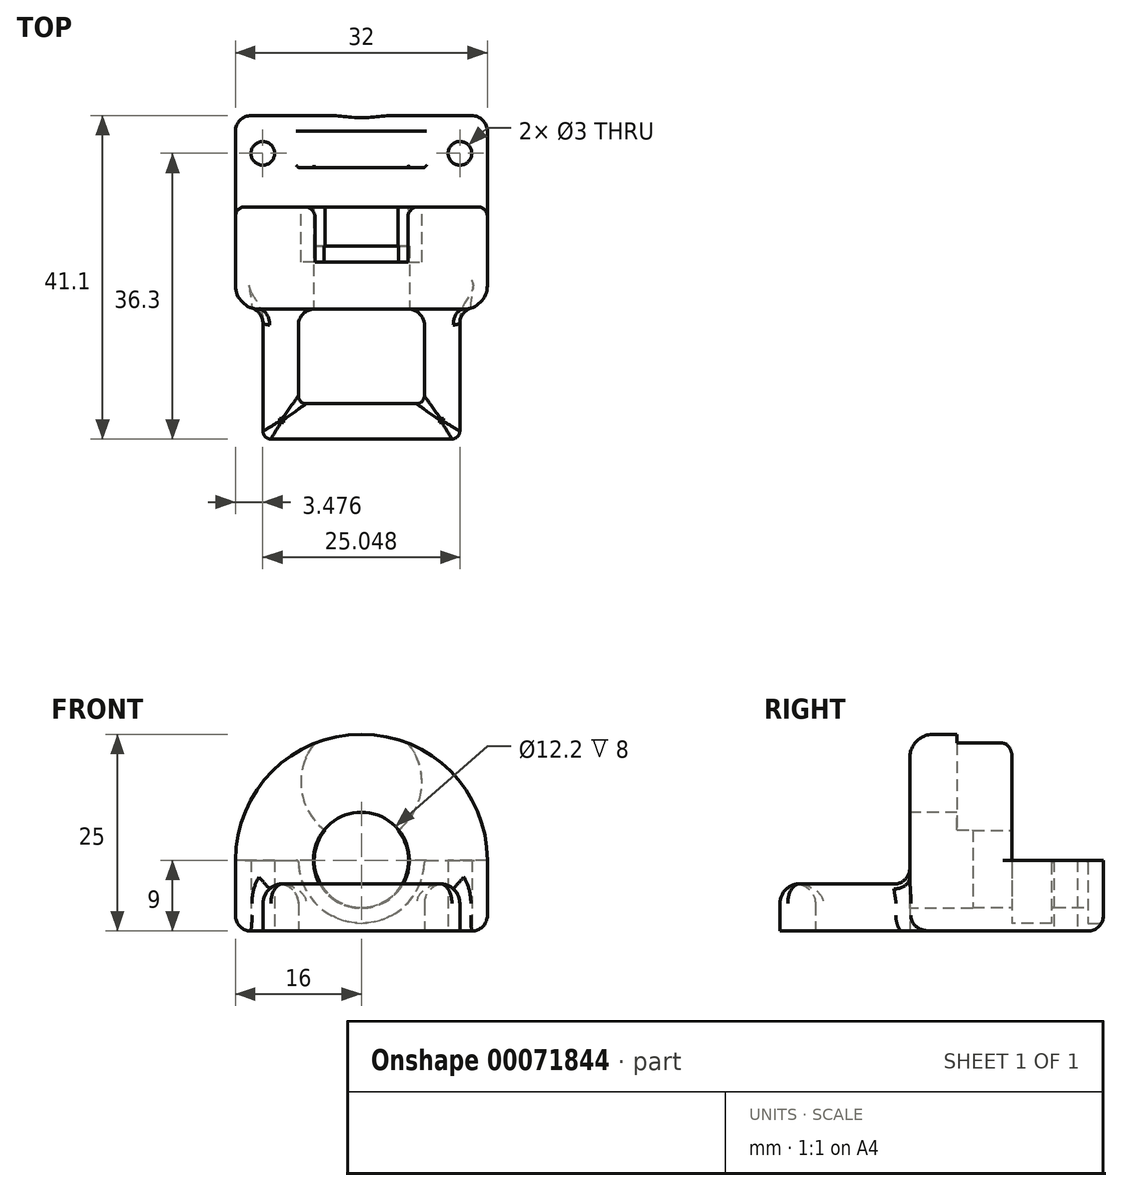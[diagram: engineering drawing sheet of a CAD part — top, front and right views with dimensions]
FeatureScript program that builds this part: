
annotation { "Feature Type Name" : "Feature", "Feature Type Description" : "" }
export const myFeature = defineFeature(function(context is Context, id is Id, definition is map)
    precondition{}
    {
        {
            var Q0;
            Q0=qCreatedBy(makeId("Top.planeOp"),FACE);
            var sketch = newSketch(context, id + "F0", { "sketchPlane" : qUnion([Q0])});
            skLineSegment(sketch, "E0.rect.bottom", {"start": v(-16, 5.8) * mm, "end": v(16, 5.8) * mm});
            skLineSegment(sketch, "E0.rect.top", {"start": v(-16, -5.8) * mm, "end": v(16, -5.8) * mm});
            skLineSegment(sketch, "E0.rect.left", {"start": v(-16, 5.8) * mm, "end": v(-16, -5.8) * mm});
            skLineSegment(sketch, "E0.rect.right", {"start": v(16, 5.8) * mm, "end": v(16, -5.8) * mm});
            skPoint(sketch, "E0.rect.middle", {"position": v(0, 0) * mm});
            skCircle(sketch, "E1", {"center": v(12.52, 1) * mm, "radius": 1.5 * mm});
            skCircle(sketch, "E2", {"center": v(-12.52, 1) * mm, "radius": 1.5 * mm});
            skSolve(sketch);
        }
        {
            var Q0;
            Q0=makeQuery(id+"F0.imprint","IMPRINT",FACE,{"disambiguationData":[TD([[makeQuery(id+"F0.imprint","IMPRINT",EDGE,{"derivedFrom":sQuery(id+"F0.wireOp",EDGE,"E0.rect.bottom")}),-1.0]])]});
            extrude(context, id + "F1", {"entities" : qUnion([Q0]), "depth" : 9 * mm});
        }
        {
            var Q0;
            Q0=makeQuery(id+"F1.opExtrude","SWEPT_FACE",FACE,{"disambiguationData":[OSD([sQuery(id+"F0.wireOp",EDGE,"E0.rect.top")])]});
            var sketch = newSketch(context, id + "F2", { "sketchPlane" : qUnion([Q0])});
            skCircle(sketch, "E3", {"center": v(0, 9) * mm, "radius": 8 * mm});
            skSolve(sketch);
        }
        {
            var Q0;
            Q0=qSketchRegion(id+"F2",true);
            var Q1;
            Q1=makeQuery(id+"F1.opExtrude","SWEPT_FACE",FACE,{"disambiguationData":[OSD([sQuery(id+"F0.wireOp",EDGE,"E0.rect.bottom")])]});
            extrude(context, id + "F3", {"entities" : qUnion([Q0, Q1]), "operationType" : NewBodyOperationType.REMOVE, "oppositeDirection" : true, "depth" : 5 * mm});
        }
        {
            var Q0;
            Q0=makeQuery(id+"F1.opExtrude","SWEPT_FACE",FACE,{"disambiguationData":[OSD([sQuery(id+"F0.wireOp",EDGE,"E0.rect.bottom")])]});
            var sketch = newSketch(context, id + "F4", { "sketchPlane" : qUnion([Q0])});
            skCircle(sketch, "E4", {"center": v(0, 9) * mm, "radius": 8 * mm});
            skSolve(sketch);
        }
        {
            var Q0;
            Q0=qSketchRegion(id+"F4",true);
            extrude(context, id + "F5", {"entities" : qUnion([Q0]), "operationType" : NewBodyOperationType.REMOVE, "oppositeDirection" : true, "depth" : 2 * mm});
        }
        {
            var Q0;
            Q0=makeQuery(id+"F5.boolean.opBoolean","COPY",FACE,{"derivedFrom":makeQuery(id+"F5.opExtrude","CAP_FACE",FACE,{"disambiguationData":[OSD([sQuery(id+"F4.wireOp",EDGE,"E4")])],"isStart":false})});
            var sketch = newSketch(context, id + "F6", { "sketchPlane" : qUnion([Q0])});
            skCircle(sketch, "E5", {"center": v(0, 9) * mm, "radius": 6 * mm});
            skSolve(sketch);
        }
        {
            var Q0;
            Q0=qSketchRegion(id+"F6",true);
            extrude(context, id + "F7", {"entities" : qUnion([Q0]), "operationType" : NewBodyOperationType.REMOVE, "oppositeDirection" : true, "depth" : 25 * mm});
        }
        {
            var Q0;
            Q0=makeQuery(id+"F1.opExtrude","SWEPT_FACE",FACE,{"disambiguationData":[OSD([sQuery(id+"F0.wireOp",EDGE,"E0.rect.top")])]});
            var sketch = newSketch(context, id + "F8", { "sketchPlane" : qUnion([Q0])});
            skArc(sketch, "E6", {"start": v(16, 9) * mm, "mid": v(0, 25) * mm, "end": v(-16, 9) * mm});
            skLineSegment(sketch, "E7", {"start": v(0, 0) * mm, "end": v(13.23, 0) * mm});
            skLineSegment(sketch, "E8", {"start": v(-13.23, 0) * mm, "end": v(0, 0) * mm});
            skLineSegment(sketch, "E9", {"start": v(-16, 9) * mm, "end": v(-16, 0) * mm});
            skLineSegment(sketch, "E10", {"start": v(16, 9) * mm, "end": v(16, 0) * mm});
            skLineSegment(sketch, "E11", {"start": v(-16, 0) * mm, "end": v(16, 0) * mm});
            skSolve(sketch);
        }
        {
            var Q0;
            Q0=qSketchRegion(id+"F8",true);
            extrude(context, id + "F9", {"entities" : qUnion([Q0]), "operationType" : NewBodyOperationType.ADD, "depth" : 13 * mm});
        }
        {
            var Q0;
            Q0=qCreatedBy(makeId("Top.planeOp"),FACE);
            var sketch = newSketch(context, id + "F10", { "sketchPlane" : qUnion([Q0])});
            skLineSegment(sketch, "E12", {"start": v(-8, -18.8) * mm, "end": v(-12.5, -18.8) * mm});
            skLineSegment(sketch, "E13", {"start": v(-12.5, -18.8) * mm, "end": v(-8, -18.8) * mm});
            skLineSegment(sketch, "E14", {"start": v(12.5, -18.8) * mm, "end": v(12.5, -35.3) * mm});
            skLineSegment(sketch, "E15", {"start": v(12.5, -35.3) * mm, "end": v(-12.5, -35.3) * mm});
            skLineSegment(sketch, "E16", {"start": v(-12.5, -35.3) * mm, "end": v(-12.5, -18.8) * mm});
            skLineSegment(sketch, "E17", {"start": v(-8, -18.8) * mm, "end": v(-8, -30.8) * mm});
            skLineSegment(sketch, "E18", {"start": v(-8, -30.8) * mm, "end": v(8, -30.8) * mm});
            skLineSegment(sketch, "E19", {"start": v(8, -30.8) * mm, "end": v(8, -18.8) * mm});
            skLineSegment(sketch, "E20.trimOffspring", {"start": v(8, -18.8) * mm, "end": v(12.5, -18.8) * mm});
            skPoint(sketch, "E21.orphan", {"position": v(0, -18.8) * mm});
            skPoint(sketch, "E22", {"position": v(0, -30.8) * mm});
            skPoint(sketch, "E23", {"position": v(0, -35.3) * mm});
            skSolve(sketch);
        }
        {
            var Q0;
            Q0=qSketchRegion(id+"F10",true);
            extrude(context, id + "F11", {"entities" : qUnion([Q0]), "operationType" : NewBodyOperationType.ADD, "depth" : 6 * mm});
        }
        {
            var Q0;
            Q0=makeQuery(id+"F11.opExtrude","CAP_EDGE",EDGE,{"disambiguationData":[OSD([sQuery(id+"F10.wireOp",EDGE,"E17")])],"isStart":false});
            var Q1;
            Q1=makeQuery(id+"F11.opExtrude","CAP_EDGE",EDGE,{"disambiguationData":[OSD([sQuery(id+"F10.wireOp",EDGE,"E16")])],"isStart":false});
            var Q2;
            Q2=makeQuery(id+"F11.opExtrude","CAP_EDGE",EDGE,{"disambiguationData":[OSD([sQuery(id+"F10.wireOp",EDGE,"E19")])],"isStart":false});
            var Q3;
            Q3=makeQuery(id+"F11.opExtrude","CAP_EDGE",EDGE,{"disambiguationData":[OSD([sQuery(id+"F10.wireOp",EDGE,"E14")])],"isStart":false});
            var Q4;
            Q4=makeQuery(id+"F11.opExtrude","CAP_EDGE",EDGE,{"disambiguationData":[OSD([sQuery(id+"F10.wireOp",EDGE,"E18")])],"isStart":false});
            var Q5;
            Q5=makeQuery(id+"F11.opExtrude","CAP_EDGE",EDGE,{"disambiguationData":[OSD([sQuery(id+"F10.wireOp",EDGE,"E15")])],"isStart":false});
            fillet(context, id + "F12", {"entities" : qUnion([Q0, Q1, Q2, Q3, Q4, Q5]), "radius" : 2.5 * mm, "tangentPropagation" : true, "allowEdgeOverflow" : false});
        }
        {
            var Q0;
            Q0=makeQuery(id+"F9.opExtrude","CAP_EDGE",EDGE,{"disambiguationData":[OSD([sQuery(id+"F8.wireOp",EDGE,"E6")])],"isStart":false});
            fillet(context, id + "F13", {"entities" : qUnion([Q0]), "radius" : 3 * mm, "tangentPropagation" : true, "allowEdgeOverflow" : false});
        }
        {
            var Q0;
            Q0=makeQuery(id+"F9.opExtrude","CAP_EDGE",EDGE,{"disambiguationData":[OSD([sQuery(id+"F8.wireOp",EDGE,"E6")])],"isStart":true});
            fillet(context, id + "F14", {"entities" : qUnion([Q0]), "radius" : 1.2 * mm, "tangentPropagation" : true, "allowEdgeOverflow" : false});
        }
        {
            var Q0;
            Q0=makeQuery(id+"F9.opExtrude","CAP_FACE",FACE,{"disambiguationData":[OSD([sQuery(id+"F8.wireOp",EDGE,"E6"),sQuery(id+"F8.wireOp",EDGE,"E9"),sQuery(id+"F8.wireOp",EDGE,"E10"),sQuery(id+"F8.wireOp",EDGE,"E11")])],"isStart":false});
            var sketch = newSketch(context, id + "F15", { "sketchPlane" : qUnion([Q0])});
            skCircle(sketch, "E24", {"center": v(0, 9) * mm, "radius": 6.1 * mm});
            skSolve(sketch);
        }
        {
            var Q0;
            Q0=qSketchRegion(id+"F15",true);
            extrude(context, id + "F16", {"entities" : qUnion([Q0]), "operationType" : NewBodyOperationType.REMOVE, "oppositeDirection" : true, "depth" : 8 * mm});
        }
        {
            var Q0;
            Q0=makeQuery(id+"F13.opFillet","BLEND_EDGE",EDGE,{"blendedFrom":[makeQuery(id+"F9.opExtrude","CAP_EDGE",EDGE,{"disambiguationData":[OSD([sQuery(id+"F8.wireOp",EDGE,"E9")])],"isStart":false}),makeQuery(id+"F9.boolean.opBoolean","MERGE",FACE,{"derivedFrom":[makeQuery(id+"F1.opExtrude","CAP_FACE",FACE,{"disambiguationData":[OSD([sQuery(id+"F0.wireOp",EDGE,"E0.rect.bottom"),sQuery(id+"F0.wireOp",EDGE,"E0.rect.top"),sQuery(id+"F0.wireOp",EDGE,"E0.rect.left"),sQuery(id+"F0.wireOp",EDGE,"E0.rect.right"),sQuery(id+"F0.wireOp",EDGE,"E1"),sQuery(id+"F0.wireOp",EDGE,"E2")])],"isStart":true}),makeQuery(id+"F9.opExtrude","SWEPT_FACE",FACE,{"disambiguationData":[OSD([sQuery(id+"F8.wireOp",EDGE,"E11")])]})]})],"blendedInto":[makeQuery(id+"F9.boolean.opBoolean","MERGE",FACE,{"derivedFrom":[makeQuery(id+"F1.opExtrude","CAP_FACE",FACE,{"disambiguationData":[OSD([sQuery(id+"F0.wireOp",EDGE,"E0.rect.bottom"),sQuery(id+"F0.wireOp",EDGE,"E0.rect.top"),sQuery(id+"F0.wireOp",EDGE,"E0.rect.left"),sQuery(id+"F0.wireOp",EDGE,"E0.rect.right"),sQuery(id+"F0.wireOp",EDGE,"E1"),sQuery(id+"F0.wireOp",EDGE,"E2")])],"isStart":true}),makeQuery(id+"F9.opExtrude","SWEPT_FACE",FACE,{"disambiguationData":[OSD([sQuery(id+"F8.wireOp",EDGE,"E11")])]})]})]});
            fillet(context, id + "F17", {"entities" : qUnion([Q0]), "radius" : 2 * mm, "tangentPropagation" : true, "allowEdgeOverflow" : false});
        }
        {
            var Q0;
            {var subQ0=sQuery(id+"F8.wireOp",EDGE,"E6");var subQ1=sQuery(id+"F8.wireOp",EDGE,"E9");var subQ2=sQuery(id+"F8.wireOp",EDGE,"E10");Q0=makeQuery(id+"F9.boolean.opBoolean","SPLIT",FACE,{"disambiguationData":[TD([makeQuery(id+"F3.boolean.opBoolean","COPY",FACE,{"derivedFrom":makeQuery(id+"F3.opExtrude","SWEPT_FACE",FACE,{"disambiguationData":[OSD([sQuery(id+"F2.wireOp",EDGE,"E3")])]})})])],"derivedFrom":makeQuery(id+"F9.opExtrude","CAP_FACE",FACE,{"disambiguationData":[OSD([subQ0,subQ1,subQ2,sQuery(id+"F8.wireOp",EDGE,"E11")])],"isStart":true})});}
            var sketch = newSketch(context, id + "F18", { "sketchPlane" : qUnion([Q0])});
            skCircle(sketch, "E25", {"center": v(0, 9) * mm, "radius": 6 * mm});
            skCircle(sketch, "E26", {"center": v(0, 18.94) * mm, "radius": 7.69 * mm});
            skSolve(sketch);
        }
        {
            var Q0;
            Q0=makeQuery(id+"F1.opExtrude","CAP_EDGE",EDGE,{"disambiguationData":[OSD([sQuery(id+"F0.wireOp",EDGE,"E0.rect.bottom")])],"isStart":true});
            var Q1;
            Q1=makeQuery(id+"F7.boolean.opBoolean","COPY",EDGE,{"derivedFrom":makeQuery(id+"F7.opExtrude","CAP_EDGE",EDGE,{"disambiguationData":[OSD([sQuery(id+"F6.wireOp",EDGE,"E5")])],"isStart":true})});
            var Q2;
            Q2=makeQuery(id+"F1.opExtrude","SWEPT_EDGE",EDGE,{"disambiguationData":[OSD([sQuery(id+"F0.wireOp",EDGE,"E0.rect.bottom"),sQuery(id+"F0.wireOp",EDGE,"E0.rect.left")])]});
            var Q3;
            Q3=makeQuery(id+"F1.opExtrude","CAP_EDGE",EDGE,{"disambiguationData":[OSD([sQuery(id+"F0.wireOp",EDGE,"E0.rect.left")])],"isStart":true});
            var Q4;
            Q4=makeQuery(id+"F1.opExtrude","SWEPT_EDGE",EDGE,{"disambiguationData":[OSD([sQuery(id+"F0.wireOp",EDGE,"E0.rect.bottom"),sQuery(id+"F0.wireOp",EDGE,"E0.rect.right")])]});
            var Q5;
            Q5=makeQuery(id+"F1.opExtrude","CAP_EDGE",EDGE,{"disambiguationData":[OSD([sQuery(id+"F0.wireOp",EDGE,"E0.rect.right")])],"isStart":true});
            fillet(context, id + "F19", {"entities" : qUnion([Q0, Q1, Q2, Q3, Q4, Q5]), "radius" : 2 * mm, "tangentPropagation" : true, "allowEdgeOverflow" : false});
        }
        {
            var Q0;
            Q0=qSketchRegion(id+"F18",true);
            extrude(context, id + "F20", {"entities" : qUnion([Q0]), "operationType" : NewBodyOperationType.REMOVE, "oppositeDirection" : true, "depth" : 7 * mm});
        }
        {
            var Q0;
            Q0=makeQuery(id+"F12.opFillet","BLEND_EDGE",EDGE,{"blendedFrom":[makeQuery(id+"F11.opExtrude","CAP_EDGE",EDGE,{"disambiguationData":[OSD([sQuery(id+"F10.wireOp",EDGE,"E14")])],"isStart":false}),makeQuery(id+"F11.opExtrude","CAP_EDGE",EDGE,{"disambiguationData":[OSD([sQuery(id+"F10.wireOp",EDGE,"E15")])],"isStart":false})],"blendedInto":[]});
            var Q1;
            Q1=makeQuery(id+"F12.opFillet","BLEND_EDGE",EDGE,{"blendedFrom":[makeQuery(id+"F11.opExtrude","CAP_EDGE",EDGE,{"disambiguationData":[OSD([sQuery(id+"F10.wireOp",EDGE,"E18")])],"isStart":false}),makeQuery(id+"F11.opExtrude","CAP_EDGE",EDGE,{"disambiguationData":[OSD([sQuery(id+"F10.wireOp",EDGE,"E19")])],"isStart":false})],"blendedInto":[]});
            var Q2;
            Q2=makeQuery(id+"F12.opFillet","BLEND_EDGE",EDGE,{"blendedFrom":[makeQuery(id+"F11.opExtrude","CAP_EDGE",EDGE,{"disambiguationData":[OSD([sQuery(id+"F10.wireOp",EDGE,"E14")])],"isStart":false}),makeQuery(id+"F11.opExtrude","CAP_EDGE",EDGE,{"disambiguationData":[OSD([sQuery(id+"F10.wireOp",EDGE,"E19")])],"isStart":false})],"blendedInto":[]});
            var Q3;
            Q3=makeQuery(id+"F12.opFillet","BLEND_EDGE",EDGE,{"blendedFrom":[makeQuery(id+"F11.opExtrude","CAP_EDGE",EDGE,{"disambiguationData":[OSD([sQuery(id+"F10.wireOp",EDGE,"E15")])],"isStart":false}),makeQuery(id+"F11.opExtrude","CAP_EDGE",EDGE,{"disambiguationData":[OSD([sQuery(id+"F10.wireOp",EDGE,"E18")])],"isStart":false})],"blendedInto":[]});
            var Q4;
            Q4=makeQuery(id+"F12.opFillet","BLEND_EDGE",EDGE,{"blendedFrom":[makeQuery(id+"F11.opExtrude","CAP_EDGE",EDGE,{"disambiguationData":[OSD([sQuery(id+"F10.wireOp",EDGE,"E16")])],"isStart":false}),makeQuery(id+"F11.opExtrude","CAP_EDGE",EDGE,{"disambiguationData":[OSD([sQuery(id+"F10.wireOp",EDGE,"E17")])],"isStart":false})],"blendedInto":[]});
            var Q5;
            Q5=makeQuery(id+"F12.opFillet","BLEND_EDGE",EDGE,{"blendedFrom":[makeQuery(id+"F11.opExtrude","CAP_EDGE",EDGE,{"disambiguationData":[OSD([sQuery(id+"F10.wireOp",EDGE,"E15")])],"isStart":false}),makeQuery(id+"F11.opExtrude","CAP_EDGE",EDGE,{"disambiguationData":[OSD([sQuery(id+"F10.wireOp",EDGE,"E16")])],"isStart":false})],"blendedInto":[]});
            var Q6;
            Q6=makeQuery(id+"F12.opFillet","BLEND_EDGE",EDGE,{"blendedFrom":[makeQuery(id+"F11.opExtrude","CAP_EDGE",EDGE,{"disambiguationData":[OSD([sQuery(id+"F10.wireOp",EDGE,"E17")])],"isStart":false}),makeQuery(id+"F11.opExtrude","CAP_EDGE",EDGE,{"disambiguationData":[OSD([sQuery(id+"F10.wireOp",EDGE,"E18")])],"isStart":false})],"blendedInto":[]});
            fillet(context, id + "F21", {"entities" : qUnion([Q0, Q1, Q2, Q3, Q4, Q5, Q6]), "radius" : 1 * mm, "tangentPropagation" : true, "allowEdgeOverflow" : false});
        }
        {
            var Q0;
            Q0=makeQuery(id+"F12.opFillet","BLEND_EDGE",EDGE,{"blendedFrom":[makeQuery(id+"F11.opExtrude","CAP_EDGE",EDGE,{"disambiguationData":[OSD([sQuery(id+"F10.wireOp",EDGE,"E14")])],"isStart":false}),makeQuery(id+"F9.opExtrude","CAP_FACE",FACE,{"disambiguationData":[OSD([sQuery(id+"F8.wireOp",EDGE,"E6"),sQuery(id+"F8.wireOp",EDGE,"E9"),sQuery(id+"F8.wireOp",EDGE,"E10"),sQuery(id+"F8.wireOp",EDGE,"E11")])],"isStart":false})],"blendedInto":[makeQuery(id+"F9.opExtrude","CAP_FACE",FACE,{"disambiguationData":[OSD([sQuery(id+"F8.wireOp",EDGE,"E6"),sQuery(id+"F8.wireOp",EDGE,"E9"),sQuery(id+"F8.wireOp",EDGE,"E10"),sQuery(id+"F8.wireOp",EDGE,"E11")])],"isStart":false})]});
            var Q1;
            Q1=makeQuery(id+"F12.opFillet","BLEND_EDGE",EDGE,{"blendedFrom":[makeQuery(id+"F11.opExtrude","CAP_EDGE",EDGE,{"disambiguationData":[OSD([sQuery(id+"F10.wireOp",EDGE,"E17")])],"isStart":false}),makeQuery(id+"F9.opExtrude","CAP_FACE",FACE,{"disambiguationData":[OSD([sQuery(id+"F8.wireOp",EDGE,"E6"),sQuery(id+"F8.wireOp",EDGE,"E9"),sQuery(id+"F8.wireOp",EDGE,"E10"),sQuery(id+"F8.wireOp",EDGE,"E11")])],"isStart":false})],"blendedInto":[makeQuery(id+"F9.opExtrude","CAP_FACE",FACE,{"disambiguationData":[OSD([sQuery(id+"F8.wireOp",EDGE,"E6"),sQuery(id+"F8.wireOp",EDGE,"E9"),sQuery(id+"F8.wireOp",EDGE,"E10"),sQuery(id+"F8.wireOp",EDGE,"E11")])],"isStart":false})]});
            fillet(context, id + "F22", {"entities" : qUnion([Q0, Q1]), "radius" : 2 * mm, "tangentPropagation" : true, "allowEdgeOverflow" : false});
        }
        {
            var Q0;
            Q0=makeQuery(id+"F3.boolean.opBoolean","INTERSECT",EDGE,{"disambiguationData":[OD(0.0)],"derivedFrom":[makeQuery(id+"F1.opExtrude","CAP_FACE",FACE,{"disambiguationData":[OSD([sQuery(id+"F0.wireOp",EDGE,"E0.rect.bottom"),sQuery(id+"F0.wireOp",EDGE,"E0.rect.top"),sQuery(id+"F0.wireOp",EDGE,"E0.rect.left"),sQuery(id+"F0.wireOp",EDGE,"E0.rect.right"),sQuery(id+"F0.wireOp",EDGE,"E1"),sQuery(id+"F0.wireOp",EDGE,"E2")])],"isStart":false}),makeQuery(id+"F3.opExtrude","SWEPT_FACE",FACE,{"disambiguationData":[OSD([sQuery(id+"F2.wireOp",EDGE,"E3")])]})]});
            var Q1;
            Q1=makeQuery(id+"F3.boolean.opBoolean","INTERSECT",EDGE,{"disambiguationData":[OD(1.0)],"derivedFrom":[makeQuery(id+"F1.opExtrude","CAP_FACE",FACE,{"disambiguationData":[OSD([sQuery(id+"F0.wireOp",EDGE,"E0.rect.bottom"),sQuery(id+"F0.wireOp",EDGE,"E0.rect.top"),sQuery(id+"F0.wireOp",EDGE,"E0.rect.left"),sQuery(id+"F0.wireOp",EDGE,"E0.rect.right"),sQuery(id+"F0.wireOp",EDGE,"E1"),sQuery(id+"F0.wireOp",EDGE,"E2")])],"isStart":false}),makeQuery(id+"F3.opExtrude","SWEPT_FACE",FACE,{"disambiguationData":[OSD([sQuery(id+"F2.wireOp",EDGE,"E3")])]})]});
            var Q2;
            Q2=makeQuery(id+"F7.boolean.opBoolean","INTERSECT",EDGE,{"disambiguationData":[OD(1.0)],"derivedFrom":[makeQuery(id+"F1.opExtrude","CAP_FACE",FACE,{"disambiguationData":[OSD([sQuery(id+"F0.wireOp",EDGE,"E0.rect.bottom"),sQuery(id+"F0.wireOp",EDGE,"E0.rect.top"),sQuery(id+"F0.wireOp",EDGE,"E0.rect.left"),sQuery(id+"F0.wireOp",EDGE,"E0.rect.right"),sQuery(id+"F0.wireOp",EDGE,"E1"),sQuery(id+"F0.wireOp",EDGE,"E2")])],"isStart":false}),makeQuery(id+"F7.opExtrude","SWEPT_FACE",FACE,{"disambiguationData":[OSD([sQuery(id+"F6.wireOp",EDGE,"E5")])]})]});
            var Q3;
            Q3=makeQuery(id+"F7.boolean.opBoolean","INTERSECT",EDGE,{"disambiguationData":[OD(0.0)],"derivedFrom":[makeQuery(id+"F1.opExtrude","CAP_FACE",FACE,{"disambiguationData":[OSD([sQuery(id+"F0.wireOp",EDGE,"E0.rect.bottom"),sQuery(id+"F0.wireOp",EDGE,"E0.rect.top"),sQuery(id+"F0.wireOp",EDGE,"E0.rect.left"),sQuery(id+"F0.wireOp",EDGE,"E0.rect.right"),sQuery(id+"F0.wireOp",EDGE,"E1"),sQuery(id+"F0.wireOp",EDGE,"E2")])],"isStart":false}),makeQuery(id+"F7.opExtrude","SWEPT_FACE",FACE,{"disambiguationData":[OSD([sQuery(id+"F6.wireOp",EDGE,"E5")])]})]});
            var Q4;
            Q4=makeQuery(id+"F5.boolean.opBoolean","INTERSECT",EDGE,{"disambiguationData":[OD(1.0)],"derivedFrom":[makeQuery(id+"F1.opExtrude","CAP_FACE",FACE,{"disambiguationData":[OSD([sQuery(id+"F0.wireOp",EDGE,"E0.rect.bottom"),sQuery(id+"F0.wireOp",EDGE,"E0.rect.top"),sQuery(id+"F0.wireOp",EDGE,"E0.rect.left"),sQuery(id+"F0.wireOp",EDGE,"E0.rect.right"),sQuery(id+"F0.wireOp",EDGE,"E1"),sQuery(id+"F0.wireOp",EDGE,"E2")])],"isStart":false}),makeQuery(id+"F5.opExtrude","SWEPT_FACE",FACE,{"disambiguationData":[OSD([sQuery(id+"F4.wireOp",EDGE,"E4")])]})]});
            var Q5;
            Q5=makeQuery(id+"F5.boolean.opBoolean","INTERSECT",EDGE,{"disambiguationData":[OD(0.0)],"derivedFrom":[makeQuery(id+"F1.opExtrude","CAP_FACE",FACE,{"disambiguationData":[OSD([sQuery(id+"F0.wireOp",EDGE,"E0.rect.bottom"),sQuery(id+"F0.wireOp",EDGE,"E0.rect.top"),sQuery(id+"F0.wireOp",EDGE,"E0.rect.left"),sQuery(id+"F0.wireOp",EDGE,"E0.rect.right"),sQuery(id+"F0.wireOp",EDGE,"E1"),sQuery(id+"F0.wireOp",EDGE,"E2")])],"isStart":false}),makeQuery(id+"F5.opExtrude","SWEPT_FACE",FACE,{"disambiguationData":[OSD([sQuery(id+"F4.wireOp",EDGE,"E4")])]})]});
            var Q6;
            Q6=makeQuery(id+"F7.boolean.opBoolean","INTERSECT",EDGE,{"derivedFrom":[makeQuery(id+"F3.boolean.opBoolean","COPY",FACE,{"derivedFrom":makeQuery(id+"F3.opExtrude","CAP_FACE",FACE,{"disambiguationData":[OSD([sQuery(id+"F2.wireOp",EDGE,"E3")])],"isStart":false})}),makeQuery(id+"F7.opExtrude","SWEPT_FACE",FACE,{"disambiguationData":[OSD([sQuery(id+"F6.wireOp",EDGE,"E5")])]})]});
            var Q7;
            Q7=makeQuery(id+"F7.boolean.opBoolean","SPLIT",EDGE,{"disambiguationData":[OD(0.0)],"derivedFrom":makeQuery(id+"F3.boolean.opBoolean","INTERSECT",EDGE,{"derivedFrom":[makeQuery(id+"F1.opExtrude","CAP_FACE",FACE,{"disambiguationData":[OSD([sQuery(id+"F0.wireOp",EDGE,"E0.rect.bottom"),sQuery(id+"F0.wireOp",EDGE,"E0.rect.top"),sQuery(id+"F0.wireOp",EDGE,"E0.rect.left"),sQuery(id+"F0.wireOp",EDGE,"E0.rect.right"),sQuery(id+"F0.wireOp",EDGE,"E1"),sQuery(id+"F0.wireOp",EDGE,"E2")])],"isStart":false}),makeQuery(id+"F3.opExtrude","CAP_FACE",FACE,{"disambiguationData":[OSD([sQuery(id+"F2.wireOp",EDGE,"E3")])],"isStart":false})]})});
            var Q8;
            Q8=makeQuery(id+"F7.boolean.opBoolean","SPLIT",EDGE,{"disambiguationData":[OD(1.0)],"derivedFrom":makeQuery(id+"F3.boolean.opBoolean","INTERSECT",EDGE,{"derivedFrom":[makeQuery(id+"F1.opExtrude","CAP_FACE",FACE,{"disambiguationData":[OSD([sQuery(id+"F0.wireOp",EDGE,"E0.rect.bottom"),sQuery(id+"F0.wireOp",EDGE,"E0.rect.top"),sQuery(id+"F0.wireOp",EDGE,"E0.rect.left"),sQuery(id+"F0.wireOp",EDGE,"E0.rect.right"),sQuery(id+"F0.wireOp",EDGE,"E1"),sQuery(id+"F0.wireOp",EDGE,"E2")])],"isStart":false}),makeQuery(id+"F3.opExtrude","CAP_FACE",FACE,{"disambiguationData":[OSD([sQuery(id+"F2.wireOp",EDGE,"E3")])],"isStart":false})]})});
            var Q9;
            Q9=makeQuery(id+"F20.boolean.opBoolean","COPY",EDGE,{"derivedFrom":makeQuery(id+"F20.opExtrude","CAP_EDGE",EDGE,{"disambiguationData":[OSD([sQuery(id+"F18.wireOp",EDGE,"E25")])],"isStart":true})});
            fillet(context, id + "F23", {"entities" : qUnion([Q0, Q1, Q2, Q3, Q4, Q5, Q6, Q7, Q8, Q9]), "radius" : 0.3 * mm, "allowEdgeOverflow" : false});
        }
    });
